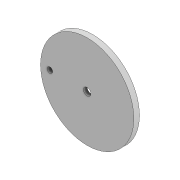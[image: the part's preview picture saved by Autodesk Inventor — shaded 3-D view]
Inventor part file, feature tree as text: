
AUTODESK INVENTOR PART (.ipt)
format: ipt  version: 2022 (Build 260153000, 153)  size: 133,632 bytes
history: native  units: mm
features: extrude x4, sketch x4, other x1, projected_geometry x1
ambient origin geometry x8: Origin, YZ Plane, XZ Plane, XY Plane, X Axis, Y Axis, Z Axis, Center Point
bodies: Body1 (feature_tree)
feature tree (10):
  other  "Sólido1"
  extrude  "Extrusión1"  Depth=3.0mm TaperAngle=0.0deg
  extrude  "Extrusión2"  Depth=3.0mm TaperAngle=0.0deg
  extrude  "Extrusión3"  Depth=20.0mm
  extrude  "Extrusión4"  Depth=1.0mm
  sketch  "Boceto1"  dims[d0=50.0mm d1=3.0mm d2=0.0mm]
  sketch  "Boceto2"  dims[d3=4.0mm d4=3.0mm d5=0.0mm]
  sketch  "Boceto3"  dims[d6=3.0mm d7=20.0mm]
  projected_geometry  "Contorno proyectado1"
  sketch  "Boceto4"  dims[d8=3.0mm d9=0.0mm d10=0.25mm d11=1.0mm d12=0.0mm]
